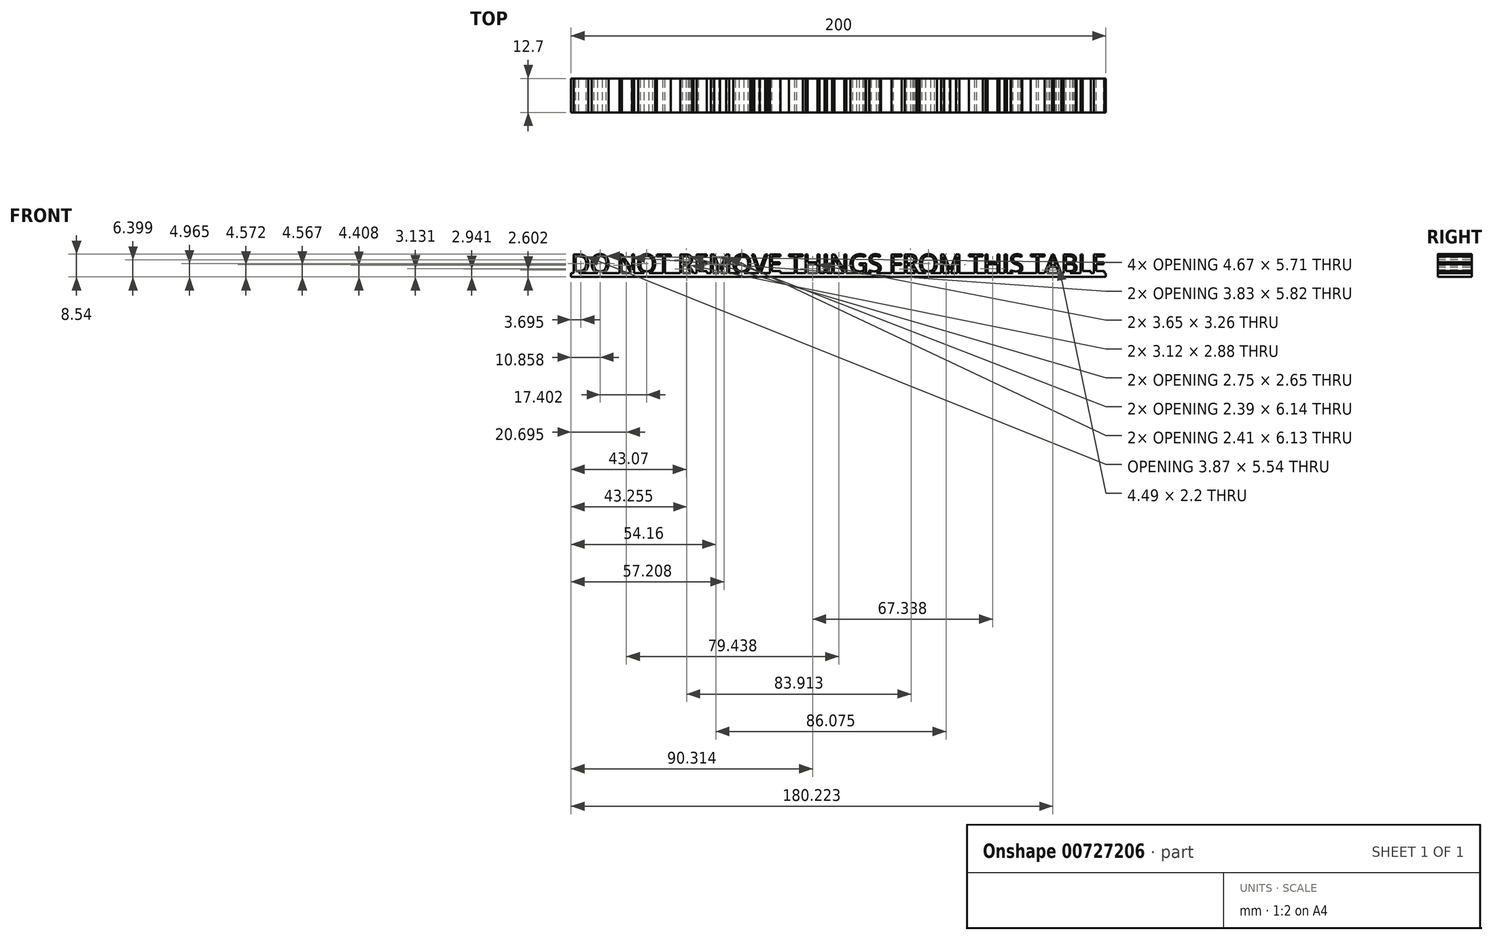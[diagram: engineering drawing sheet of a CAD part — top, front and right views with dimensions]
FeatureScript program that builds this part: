
annotation { "Feature Type Name" : "Feature", "Feature Type Description" : "" }
export const myFeature = defineFeature(function(context is Context, id is Id, definition is map)
    precondition{}
    {
        {
            var Q0;
            Q0=qCreatedBy(makeId("Front.planeOp"),FACE);
            var sketch = newSketch(context, id + "F0", { "sketchPlane" : qUnion([Q0])});
            skText(sketch, "E0", { "text": "DO NOT REMOVE THINGS FROM THIS TABLE", "fontName": "OpenSans-Regular.ttf"});
            skLineSegment(sketch, "E1.bottom", {"start": v(100, 1.5) * mm, "end": v(-100, 1.5) * mm});
            skLineSegment(sketch, "E1.top", {"start": v(100, 0) * mm, "end": v(-100, 0) * mm});
            skLineSegment(sketch, "E1.left", {"start": v(100, 1.5) * mm, "end": v(100, 0) * mm});
            skLineSegment(sketch, "E1.right", {"start": v(-100, 1.5) * mm, "end": v(-100, 0) * mm});
            const initialGuessF0  = {"E0": [-0.1, 0.0015, 1, 0, 0.00699]};
            skSetInitialGuess(sketch, initialGuessF0);
            skSolve(sketch);
        }
        {
            var Q0;
            {var subQ6=sQuery(id+"F0.wireOp",EDGE,"E0.sketch_text.stroke-401");var subQ7=sQuery(id+"F0.wireOp",EDGE,"E0.sketch_text.stroke-326");var subQ8=sQuery(id+"F0.wireOp",EDGE,"E0.sketch_text.stroke-325");var subQ9=makeQuery(id+"F0.imprint","INTERSECT",VERTEX,{"derivedFrom":[subQ8,subQ7]});var subQ13=sQuery(id+"F0.wireOp",EDGE,"E0.sketch_text.stroke-357");var subQ16=makeQuery(id+"F0.imprint","IMPRINT",EDGE,{"disambiguationData":[TD([[subQ9,1.0]])],"derivedFrom":subQ8});var subQ18=sQuery(id+"F0.wireOp",EDGE,"E0.sketch_text.stroke-61");var subQ19=sQuery(id+"F0.wireOp",EDGE,"E0.sketch_text.stroke-46");var subQ26=sQuery(id+"F0.wireOp",EDGE,"E0.sketch_text.stroke-238");var subQ27=sQuery(id+"F0.wireOp",EDGE,"E0.sketch_text.stroke-214");var subQ29=sQuery(id+"F0.wireOp",EDGE,"E0.sketch_text.stroke-308");var subQ30=makeQuery(id+"F0.imprint","IMPRINT",EDGE,{"derivedFrom":subQ29});var subQ31=sQuery(id+"F0.wireOp",EDGE,"E0.sketch_text.stroke-215");var subQ32=makeQuery(id+"F0.imprint","INTERSECT",VERTEX,{"derivedFrom":[subQ27,subQ31]});var subQ33=makeQuery(id+"F0.imprint","IMPRINT",EDGE,{"disambiguationData":[TD([[subQ32,1.0]])],"derivedFrom":subQ27});var subQ38=makeQuery(id+"F0.imprint","IMPRINT",EDGE,{"derivedFrom":subQ18});var subQ43=sQuery(id+"F0.wireOp",EDGE,"E0.sketch_text.stroke-196");var subQ44=makeQuery(id+"F0.imprint","IMPRINT",EDGE,{"derivedFrom":subQ43});var subQ48=sQuery(id+"F0.wireOp",EDGE,"E0.sketch_text.stroke-268");var subQ49=sQuery(id+"F0.wireOp",EDGE,"E0.sketch_text.stroke-267");var subQ50=makeQuery(id+"F0.imprint","INTERSECT",VERTEX,{"derivedFrom":[subQ49,subQ48]});var subQ52=makeQuery(id+"F0.imprint","IMPRINT",EDGE,{"disambiguationData":[TD([[subQ50,1.0]])],"derivedFrom":subQ49});var subQ56=sQuery(id+"F0.wireOp",EDGE,"E0.sketch_text.stroke-87");var subQ57=sQuery(id+"F0.wireOp",EDGE,"E0.sketch_text.stroke-178");var subQ58=makeQuery(id+"F0.imprint","IMPRINT",EDGE,{"derivedFrom":subQ57});var subQ64=sQuery(id+"F0.wireOp",EDGE,"E0.sketch_text.stroke-349");var subQ65=makeQuery(id+"F0.imprint","IMPRINT",EDGE,{"derivedFrom":subQ64});var subQ72=sQuery(id+"F0.wireOp",EDGE,"E0.sketch_text.stroke-47");var subQ73=makeQuery(id+"F0.imprint","INTERSECT",VERTEX,{"derivedFrom":[subQ19,subQ72]});var subQ79=sQuery(id+"F0.wireOp",EDGE,"E0.sketch_text.stroke-16");var subQ80=sQuery(id+"F0.wireOp",EDGE,"E0.sketch_text.stroke-15");var subQ81=makeQuery(id+"F0.imprint","INTERSECT",VERTEX,{"derivedFrom":[subQ80,subQ79]});var subQ84=sQuery(id+"F0.wireOp",EDGE,"E0.sketch_text.stroke-30");var subQ85=makeQuery(id+"F0.imprint","IMPRINT",EDGE,{"derivedFrom":subQ84});var subQ86=sQuery(id+"F0.wireOp",EDGE,"E0.sketch_text.stroke-300");var subQ87=makeQuery(id+"F0.imprint","IMPRINT",EDGE,{"derivedFrom":subQ86});var subQ88=sQuery(id+"F0.wireOp",EDGE,"E0.sketch_text.stroke-119");var subQ89=sQuery(id+"F0.wireOp",EDGE,"E0.sketch_text.stroke-118");var subQ90=makeQuery(id+"F0.imprint","INTERSECT",VERTEX,{"derivedFrom":[subQ89,subQ88]});var subQ93=makeQuery(id+"F0.imprint","IMPRINT",EDGE,{"derivedFrom":subQ6});var subQ94=sQuery(id+"F0.wireOp",EDGE,"E0.sketch_text.stroke-2");var subQ95=makeQuery(id+"F0.imprint","IMPRINT",EDGE,{"derivedFrom":subQ94});var subQ96=makeQuery(id+"F0.imprint","IMPRINT",EDGE,{"disambiguationData":[TD([[subQ73,1.0]])],"derivedFrom":subQ19});var subQ105=makeQuery(id+"F0.imprint","IMPRINT",EDGE,{"disambiguationData":[TD([[subQ81,1.0]])],"derivedFrom":subQ80});var subQ111=makeQuery(id+"F0.imprint","IMPRINT",EDGE,{"derivedFrom":subQ56});var subQ112=sQuery(id+"F0.wireOp",EDGE,"E0.sketch_text.stroke-154");var subQ113=makeQuery(id+"F0.imprint","IMPRINT",EDGE,{"derivedFrom":subQ112});var subQ114=sQuery(id+"F0.wireOp",EDGE,"E0.sketch_text.stroke-248");var subQ122=makeQuery(id+"F0.imprint","IMPRINT",EDGE,{"derivedFrom":subQ26});var subQ129=makeQuery(id+"F0.imprint","IMPRINT",EDGE,{"disambiguationData":[TD([[subQ90,1.0]])],"derivedFrom":subQ89});var subQ131=sQuery(id+"F0.wireOp",EDGE,"E0.sketch_text.stroke-142");var subQ132=makeQuery(id+"F0.imprint","IMPRINT",EDGE,{"derivedFrom":subQ131});var subQ134=sQuery(id+"F0.wireOp",EDGE,"E0.sketch_text.stroke-395");var subQ137=sQuery(id+"F0.wireOp",EDGE,"E0.sketch_text.stroke-162");var subQ138=makeQuery(id+"F0.imprint","IMPRINT",EDGE,{"derivedFrom":subQ137});var subQ170=sQuery(id+"F0.wireOp",EDGE,"E0.sketch_text.stroke-69");var subQ177=sQuery(id+"F0.wireOp",EDGE,"E0.sketch_text.stroke-99");var subQ179=sQuery(id+"F0.wireOp",EDGE,"E0.sketch_text.stroke-282");var subQ184=sQuery(id+"F0.wireOp",EDGE,"E0.sketch_text.stroke-320");var subQ186=sQuery(id+"F0.wireOp",EDGE,"E0.sketch_text.stroke-174");var subQ191=sQuery(id+"F0.wireOp",EDGE,"E0.sketch_text.stroke-266");var subQ196=sQuery(id+"F0.wireOp",EDGE,"E0.sketch_text.stroke-117");var subQ199=sQuery(id+"F0.wireOp",EDGE,"E0.sketch_text.stroke-45");var subQ202=sQuery(id+"F0.wireOp",EDGE,"E0.sketch_text.stroke-14");var subQ205=sQuery(id+"F0.wireOp",EDGE,"E0.sketch_text.stroke-324");var subQ207=sQuery(id+"F0.wireOp",EDGE,"E0.sketch_text.stroke-213");Q0=qUnion([makeQuery(id+"F0.imprint","IMPRINT",FACE,{"disambiguationData":[TD([[subQ38,-1.0]])]}),makeQuery(id+"F0.imprint","IMPRINT",FACE,{"disambiguationData":[TD([[subQ111,-1.0]])]}),makeQuery(id+"F0.imprint","IMPRINT",FACE,{"disambiguationData":[TD([[makeQuery(id+"F0.imprint","IMPRINT",EDGE,{"derivedFrom":sQuery(id+"F0.wireOp",EDGE,"E0.sketch_text.stroke-133")}),-1.0]])]}),makeQuery(id+"F0.imprint","IMPRINT",FACE,{"disambiguationData":[TD([[subQ132,-1.0]])]}),makeQuery(id+"F0.imprint","IMPRINT",FACE,{"disambiguationData":[TD([[subQ113,-1.0]])]}),makeQuery(id+"F0.imprint","IMPRINT",FACE,{"disambiguationData":[TD([[makeQuery(id+"F0.imprint","IMPRINT",EDGE,{"derivedFrom":subQ186}),-1.0]])]}),makeQuery(id+"F0.imprint","IMPRINT",FACE,{"disambiguationData":[TD([[makeQuery(id+"F0.imprint","IMPRINT",EDGE,{"derivedFrom":sQuery(id+"F0.wireOp",EDGE,"E0.sketch_text.stroke-193")}),-1.0]])]}),makeQuery(id+"F0.imprint","IMPRINT",FACE,{"disambiguationData":[TD([[makeQuery(id+"F0.imprint","IMPRINT",EDGE,{"derivedFrom":subQ207}),-1.0]])]}),makeQuery(id+"F0.imprint","IMPRINT",FACE,{"disambiguationData":[TD([[subQ122,-1.0]])]}),makeQuery(id+"F0.imprint","IMPRINT",FACE,{"disambiguationData":[TD([[subQ87,-1.0]])]}),makeQuery(id+"F0.imprint","IMPRINT",FACE,{"disambiguationData":[TD([[makeQuery(id+"F0.imprint","IMPRINT",EDGE,{"derivedFrom":subQ184}),-1.0]])]}),makeQuery(id+"F0.imprint","IMPRINT",FACE,{"disambiguationData":[TD([[makeQuery(id+"F0.imprint","IMPRINT",EDGE,{"derivedFrom":subQ205}),-1.0]])]}),makeQuery(id+"F0.imprint","IMPRINT",FACE,{"disambiguationData":[TD([[subQ65,-1.0]])]}),makeQuery(id+"F0.imprint","IMPRINT",FACE,{"disambiguationData":[TD([[makeQuery(id+"F0.imprint","IMPRINT",EDGE,{"derivedFrom":subQ134}),-1.0]])]}),makeQuery(id+"F0.imprint","IMPRINT",FACE,{"disambiguationData":[TD([[subQ93,-1.0]])]}),makeQuery(id+"F0.imprint","IMPRINT",FACE,{"disambiguationData":[TD([[makeQuery(id+"F0.imprint","IMPRINT",EDGE,{"derivedFrom":sQuery(id+"F0.wireOp",EDGE,"E0.sketch_text.stroke-0")}),-1.0]])]}),makeQuery(id+"F0.imprint","IMPRINT",FACE,{"disambiguationData":[TD([[makeQuery(id+"F0.imprint","IMPRINT",EDGE,{"derivedFrom":subQ202}),-1.0]])]}),makeQuery(id+"F0.imprint","IMPRINT",FACE,{"disambiguationData":[TD([[subQ105,-1.0]])]}),makeQuery(id+"F0.imprint","IMPRINT",FACE,{"disambiguationData":[TD([[subQ85,-1.0]])]}),makeQuery(id+"F0.imprint","IMPRINT",FACE,{"disambiguationData":[TD([[makeQuery(id+"F0.imprint","IMPRINT",EDGE,{"derivedFrom":subQ199}),-1.0]])]}),makeQuery(id+"F0.imprint","IMPRINT",FACE,{"disambiguationData":[TD([[subQ96,-1.0]])]}),makeQuery(id+"F0.imprint","IMPRINT",FACE,{"disambiguationData":[TD([[makeQuery(id+"F0.imprint","IMPRINT",EDGE,{"derivedFrom":subQ196}),-1.0]])]}),makeQuery(id+"F0.imprint","IMPRINT",FACE,{"disambiguationData":[TD([[subQ129,-1.0]])]}),makeQuery(id+"F0.imprint","IMPRINT",FACE,{"disambiguationData":[TD([[subQ138,-1.0]])]}),makeQuery(id+"F0.imprint","IMPRINT",FACE,{"disambiguationData":[TD([[subQ58,-1.0]])]}),makeQuery(id+"F0.imprint","IMPRINT",FACE,{"disambiguationData":[TD([[subQ44,-1.0]])]}),makeQuery(id+"F0.imprint","IMPRINT",FACE,{"disambiguationData":[TD([[subQ33,-1.0]])]}),makeQuery(id+"F0.imprint","IMPRINT",FACE,{"disambiguationData":[TD([[makeQuery(id+"F0.imprint","IMPRINT",EDGE,{"derivedFrom":subQ191}),-1.0]])]}),makeQuery(id+"F0.imprint","IMPRINT",FACE,{"disambiguationData":[TD([[subQ52,-1.0]])]}),makeQuery(id+"F0.imprint","IMPRINT",FACE,{"disambiguationData":[TD([[subQ30,-1.0]])]}),makeQuery(id+"F0.imprint","IMPRINT",FACE,{"disambiguationData":[TD([[subQ16,-1.0]])]}),makeQuery(id+"F0.imprint","IMPRINT",FACE,{"disambiguationData":[TD([[makeQuery(id+"F0.imprint","IMPRINT",EDGE,{"derivedFrom":subQ170}),-1.0]])]}),makeQuery(id+"F0.imprint","IMPRINT",FACE,{"disambiguationData":[TD([[makeQuery(id+"F0.imprint","IMPRINT",EDGE,{"derivedFrom":subQ177}),-1.0]])]}),makeQuery(id+"F0.imprint","IMPRINT",FACE,{"disambiguationData":[TD([[makeQuery(id+"F0.imprint","IMPRINT",EDGE,{"derivedFrom":subQ114}),-1.0]])]}),makeQuery(id+"F0.imprint","IMPRINT",FACE,{"disambiguationData":[TD([[makeQuery(id+"F0.imprint","IMPRINT",EDGE,{"derivedFrom":subQ179}),-1.0]])]}),makeQuery(id+"F0.imprint","IMPRINT",FACE,{"disambiguationData":[TD([[makeQuery(id+"F0.imprint","IMPRINT",EDGE,{"derivedFrom":subQ13}),-1.0]])]}),makeQuery(id+"F0.imprint","IMPRINT",FACE,{"disambiguationData":[TD([[makeQuery(id+"F0.imprint","IMPRINT",EDGE,{"derivedFrom":sQuery(id+"F0.wireOp",EDGE,"E0.sketch_text.stroke-370")}),-1.0]])]}),makeQuery(id+"F0.imprint","IMPRINT",FACE,{"disambiguationData":[TD([[subQ95,1.0]])]})]);}
            extrude(context, id + "F1", {"entities" : qUnion([Q0]), "depth" : 12.7 * mm, "offsetDistance" : 25.4 * mm});
        }
    });
